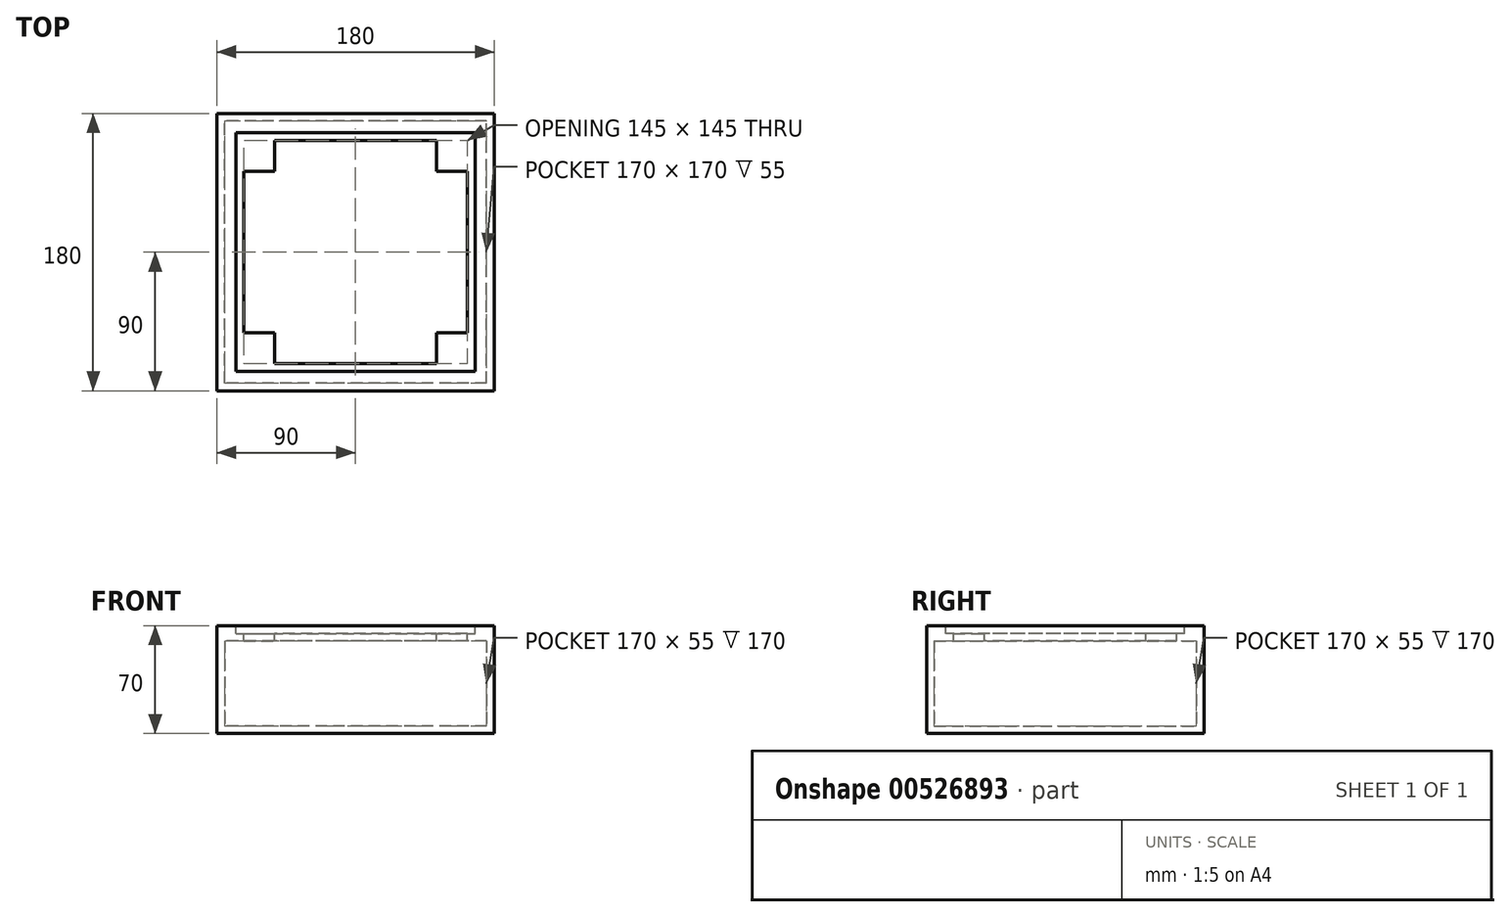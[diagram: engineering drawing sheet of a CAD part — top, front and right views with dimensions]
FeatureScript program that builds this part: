
annotation { "Feature Type Name" : "Feature", "Feature Type Description" : "" }
export const myFeature = defineFeature(function(context is Context, id is Id, definition is map)
    precondition{}
    {
        {
            var Q0;
            Q0=qCreatedBy(makeId("Top.planeOp"),FACE);
            var sketch = newSketch(context, id + "F0", { "sketchPlane" : qUnion([Q0])});
            skLineSegment(sketch, "E0.bottom", {"start": v(90, -90) * mm, "end": v(-90, -90) * mm});
            skLineSegment(sketch, "E0.top", {"start": v(90, 90) * mm, "end": v(-90, 90) * mm});
            skLineSegment(sketch, "E0.left", {"start": v(90, -90) * mm, "end": v(90, 90) * mm});
            skLineSegment(sketch, "E0.right", {"start": v(-90, -90) * mm, "end": v(-90, 90) * mm});
            skPoint(sketch, "E0.middle", {"position": v(0, 0) * mm});
            skSolve(sketch);
        }
        {
            var Q0;
            Q0=makeQuery(id+"F0.imprint","IMPRINT",FACE,{"disambiguationData":[TD([[makeQuery(id+"F0.imprint","IMPRINT",EDGE,{"derivedFrom":sQuery(id+"F0.wireOp",EDGE,"E0.bottom")}),-1.0]])]});
            extrude(context, id + "F1", {"entities" : qUnion([Q0]), "depth" : 70 * mm, "offsetDistance" : 25 * mm});
        }
        {
            var Q0;
            Q0=makeQuery(id+"F1.opExtrude","CAP_FACE",FACE,{"disambiguationData":[OSD([sQuery(id+"F0.wireOp",EDGE,"E0.bottom"),sQuery(id+"F0.wireOp",EDGE,"E0.top"),sQuery(id+"F0.wireOp",EDGE,"E0.left"),sQuery(id+"F0.wireOp",EDGE,"E0.right")])],"isStart":false});
            shell(context, id + "F2", {"entities" : qUnion([Q0]), "thickness" : 5 * mm});
        }
        {
            var Q0;
            Q0=makeQuery(id+"F1.opExtrude","CAP_FACE",FACE,{"disambiguationData":[OSD([sQuery(id+"F0.wireOp",EDGE,"E0.bottom"),sQuery(id+"F0.wireOp",EDGE,"E0.top"),sQuery(id+"F0.wireOp",EDGE,"E0.left"),sQuery(id+"F0.wireOp",EDGE,"E0.right")])],"isStart":false});
            var sketch = newSketch(context, id + "F3", { "sketchPlane" : qUnion([Q0])});
            skLineSegment(sketch, "E1.bottom", {"start": v(-85, 85) * mm, "end": v(85, 85) * mm});
            skLineSegment(sketch, "E1.top", {"start": v(-85, -85) * mm, "end": v(85, -85) * mm});
            skLineSegment(sketch, "E1.left", {"start": v(-85, 85) * mm, "end": v(-85, -85) * mm});
            skLineSegment(sketch, "E1.right", {"start": v(85, 85) * mm, "end": v(85, -85) * mm});
            skPoint(sketch, "E1.middle", {"position": v(0, 0) * mm});
            skSolve(sketch);
        }
        {
            var Q0;
            Q0 = qSketchRegion(id + "F3", true);
            extrude(context, id + "F4", {"entities" : qUnion([Q0]), "operationType" : NewBodyOperationType.ADD, "oppositeDirection" : true, "depth" : 10 * mm, "offsetDistance" : 25 * mm});
        }
        {
            var Q0;
            Q0=makeQuery(id+"F4.boolean.opBoolean","MERGE",FACE,{"derivedFrom":[makeQuery(id+"F1.opExtrude","CAP_FACE",FACE,{"disambiguationData":[OSD([sQuery(id+"F0.wireOp",EDGE,"E0.bottom"),sQuery(id+"F0.wireOp",EDGE,"E0.top"),sQuery(id+"F0.wireOp",EDGE,"E0.left"),sQuery(id+"F0.wireOp",EDGE,"E0.right")])],"isStart":false}),makeQuery(id+"F4.opExtrude","CAP_FACE",FACE,{"disambiguationData":[OSD([sQuery(id+"F3.wireOp",EDGE,"E1.bottom"),sQuery(id+"F3.wireOp",EDGE,"E1.top"),sQuery(id+"F3.wireOp",EDGE,"E1.left"),sQuery(id+"F3.wireOp",EDGE,"E1.right")])],"isStart":true})]});
            var sketch = newSketch(context, id + "F5", { "sketchPlane" : qUnion([Q0])});
            skLineSegment(sketch, "E2.bottom", {"start": v(-77.5, 77.5) * mm, "end": v(77.5, 77.5) * mm});
            skLineSegment(sketch, "E2.top", {"start": v(-77.5, -77.5) * mm, "end": v(77.5, -77.5) * mm});
            skLineSegment(sketch, "E2.left", {"start": v(-77.5, 77.5) * mm, "end": v(-77.5, -77.5) * mm});
            skLineSegment(sketch, "E2.right", {"start": v(77.5, 77.5) * mm, "end": v(77.5, -77.5) * mm});
            skPoint(sketch, "E2.middle", {"position": v(0, 0) * mm});
            skSolve(sketch);
        }
        {
            var Q0;
            Q0 = qSketchRegion(id + "F5", true);
            var Q1;
            Q1=makeQuery(id+"F5.imprint","IMPRINT",FACE,{"disambiguationData":[TD([[makeQuery(id+"F5.imprint","IMPRINT",EDGE,{"derivedFrom":sQuery(id+"F5.wireOp",EDGE,"E2.bottom")}),-1.0]])]});
            extrude(context, id + "F6", {"entities" : qUnion([Q0, Q1]), "operationType" : NewBodyOperationType.REMOVE, "oppositeDirection" : true, "depth" : 5 * mm, "offsetDistance" : 25 * mm});
        }
        {
            var Q0;
            Q0=makeQuery(id+"F6.boolean.opBoolean","COPY",FACE,{"derivedFrom":makeQuery(id+"F6.opExtrude","CAP_FACE",FACE,{"disambiguationData":[OSD([sQuery(id+"F5.wireOp",EDGE,"E2.bottom"),sQuery(id+"F5.wireOp",EDGE,"E2.top"),sQuery(id+"F5.wireOp",EDGE,"E2.left"),sQuery(id+"F5.wireOp",EDGE,"E2.right")])],"isStart":false})});
            var sketch = newSketch(context, id + "F7", { "sketchPlane" : qUnion([Q0])});
            skLineSegment(sketch, "E3.bottom", {"start": v(72.5, 72.5) * mm, "end": v(-72.5, 72.5) * mm});
            skLineSegment(sketch, "E3.top", {"start": v(72.5, -72.5) * mm, "end": v(-72.5, -72.5) * mm});
            skLineSegment(sketch, "E3.left", {"start": v(72.5, 72.5) * mm, "end": v(72.5, -72.5) * mm});
            skLineSegment(sketch, "E3.right", {"start": v(-72.5, 72.5) * mm, "end": v(-72.5, -72.5) * mm});
            skPoint(sketch, "E3.middle", {"position": v(0, 0) * mm});
            skSolve(sketch);
        }
        {
            var Q0;
            Q0=makeQuery(id+"F7.imprint","IMPRINT",FACE,{"disambiguationData":[TD([[makeQuery(id+"F7.imprint","IMPRINT",EDGE,{"derivedFrom":sQuery(id+"F7.wireOp",EDGE,"E3.bottom")}),1.0]])]});
            extrude(context, id + "F8", {"entities" : qUnion([Q0]), "operationType" : NewBodyOperationType.REMOVE, "oppositeDirection" : true, "depth" : 25 * mm, "offsetDistance" : 25 * mm});
        }
        {
            var Q0;
            Q0=makeQuery(id+"F6.boolean.opBoolean","COPY",FACE,{"derivedFrom":makeQuery(id+"F6.opExtrude","CAP_FACE",FACE,{"disambiguationData":[OSD([sQuery(id+"F5.wireOp",EDGE,"E2.bottom"),sQuery(id+"F5.wireOp",EDGE,"E2.top"),sQuery(id+"F5.wireOp",EDGE,"E2.left"),sQuery(id+"F5.wireOp",EDGE,"E2.right")])],"isStart":false})});
            var sketch = newSketch(context, id + "F9", { "sketchPlane" : qUnion([Q0])});
            skLineSegment(sketch, "E4.bottom", {"start": v(-72.5, 72.5) * mm, "end": v(-52.5, 72.5) * mm});
            skLineSegment(sketch, "E4.top", {"start": v(-72.5, 52.5) * mm, "end": v(-52.5, 52.5) * mm});
            skLineSegment(sketch, "E4.left", {"start": v(-72.5, 72.5) * mm, "end": v(-72.5, 52.5) * mm});
            skLineSegment(sketch, "E4.right", {"start": v(-52.5, 72.5) * mm, "end": v(-52.5, 52.5) * mm});
            skLineSegment(sketch, "E5.bottom", {"start": v(72.5, 72.5) * mm, "end": v(52.5, 72.5) * mm});
            skLineSegment(sketch, "E5.top", {"start": v(72.5, 52.5) * mm, "end": v(52.5, 52.5) * mm});
            skLineSegment(sketch, "E5.left", {"start": v(72.5, 72.5) * mm, "end": v(72.5, 52.5) * mm});
            skLineSegment(sketch, "E5.right", {"start": v(52.5, 72.5) * mm, "end": v(52.5, 52.5) * mm});
            skLineSegment(sketch, "E6.bottom", {"start": v(72.5, -72.5) * mm, "end": v(52.5, -72.5) * mm});
            skLineSegment(sketch, "E6.top", {"start": v(72.5, -52.5) * mm, "end": v(52.5, -52.5) * mm});
            skLineSegment(sketch, "E6.left", {"start": v(72.5, -72.5) * mm, "end": v(72.5, -52.5) * mm});
            skLineSegment(sketch, "E6.right", {"start": v(52.5, -72.5) * mm, "end": v(52.5, -52.5) * mm});
            skLineSegment(sketch, "E7.bottom", {"start": v(-72.5, -72.5) * mm, "end": v(-52.5, -72.5) * mm});
            skLineSegment(sketch, "E7.top", {"start": v(-72.5, -52.5) * mm, "end": v(-52.5, -52.5) * mm});
            skLineSegment(sketch, "E7.left", {"start": v(-72.5, -72.5) * mm, "end": v(-72.5, -52.5) * mm});
            skLineSegment(sketch, "E7.right", {"start": v(-52.5, -72.5) * mm, "end": v(-52.5, -52.5) * mm});
            skSolve(sketch);
        }
        {
            var Q0;
            Q0=makeQuery(id+"F9.imprint","IMPRINT",FACE,{"disambiguationData":[TD([[makeQuery(id+"F9.imprint","IMPRINT",EDGE,{"derivedFrom":sQuery(id+"F9.wireOp",EDGE,"E4.bottom")}),1.0]])]});
            var Q1;
            Q1=makeQuery(id+"F9.imprint","IMPRINT",FACE,{"disambiguationData":[TD([[makeQuery(id+"F9.imprint","IMPRINT",EDGE,{"derivedFrom":sQuery(id+"F9.wireOp",EDGE,"E5.bottom")}),1.0]])]});
            var Q2;
            Q2=makeQuery(id+"F9.imprint","IMPRINT",FACE,{"disambiguationData":[TD([[makeQuery(id+"F9.imprint","IMPRINT",EDGE,{"derivedFrom":sQuery(id+"F9.wireOp",EDGE,"E6.bottom")}),-1.0]])]});
            var Q3;
            Q3=makeQuery(id+"F9.imprint","IMPRINT",FACE,{"disambiguationData":[TD([[makeQuery(id+"F9.imprint","IMPRINT",EDGE,{"derivedFrom":sQuery(id+"F9.wireOp",EDGE,"E7.bottom")}),-1.0]])]});
            extrude(context, id + "F10", {"entities" : qUnion([Q0, Q1, Q2, Q3]), "operationType" : NewBodyOperationType.ADD, "oppositeDirection" : true, "depth" : 5 * mm, "offsetDistance" : 25 * mm});
        }
    });
